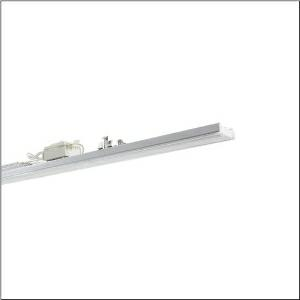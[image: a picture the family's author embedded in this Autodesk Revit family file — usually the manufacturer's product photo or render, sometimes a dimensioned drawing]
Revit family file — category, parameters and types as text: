
# Revit family: licross_r__11_recessed_ho_51te18cn4c5m_9f39
name_source: partatom
category: Lighting Fixtures
units: mm (PartAtom-declared; Revit-internal decimal feet)

## family parameters
Cut with Voids When Loaded = No
Host = Face
Light Source = No
Part Type = Normal
Room Calculation Point = No
Round Connector Dimension = Use Diameter
Shared = No

## types (1)
- --- (1 x LED, 12610 lm, 66.5 W, 4000K)
    Apparent Load = 67 VA
    CIE Flux Codes = 78 94 99 100 100
    Color Rendering = 80
    Color Temperature = 4000K
    Default Elevation = 1800 mm
    Description = Licross® 11 Recessed HO, luminaire insert, of sheet steel, galvanised, coil coated, white, length: 1.500mm, width: 66mm, height: 67mm, LED rated luminous flux: 12.610lm, light colour: 840, control gear: ON/OFF Multilumen, CLOi, with plug, 3-pole, with phase selection, mains connection: 220..240V, AC, 50/60Hz, start of lifetime: 67W, end of service life: 75W, halogen-free wiring, primary light control with lens, of plastic, primary optical cover: cover, of PMMA, light emission: direct distribution, primary light characteristic: symmetric, protection rating (complete): IP54, insulation class (complete): insulation class I (protective earthing), certification: CE, ENEC, VDE, UKCA, protection symbol: D if used in an environment with non-conductive dust loads with corresponding accessories, impact resistance: IK06, permissible ambient temperature for indoor applications: -35..+35°C, corresponds to IFS (International Featured Standards) requirements for safety and quality in the food industry, reducing of maximum allowable ambient temperature of 5°C with ceiling mounting, LABS conformity tested according to VDMA 24364:2018-05, packaging unit: 1 piece
    Height = 58 mm
    Lamp = 1 x LED
    Lamp Light Flux = 12610 lm
    Lamp Power = 66.5 W
    Lamp count = 1
    Length = 1500 mm
    Luminous efficacy = 190 lm/W
    Manufacturer = Siteco
    ModVariant = No
    Model = 51TE18CN4C5M
    Mounting Place = Ceiling
    Mounting Type = Pendant
    Number of Poles = 1
    OnlyDefault = Yes
    Power Factor = 1
    Product Name = Licross® 11 Recessed HO
    Product group = luminaire insert
    ProductGroupID = 902
    Protection Class = Protection class I
    Protection Degree = IP 54
    RLX_Detail_Level = 1
    RLX_Emergency_Light_Flux = 0 lm
    RLX_Emergency_Type = 0
    RLX_Emergency_Type_DB = No
    RlxData = <blob elided: 22309 chars, md5=1e41ee86>
    Socket = socket
    Standby Power = 0 W
    System Light Flux = 12610 lm
    System Power = 67 W
    Type Comments = factory setting: luminous flux: 100 % | (A | C | E) | 156 mA
    Type Image = l_1296930.jpg
    URL = http://relux.com
    VarID = @adj_084666
    Voltage = 0 V
    Weight = 0.00 kg
    Width = 66 mm

## geometry (parser evidence)
native form markers: Blend x4, Sweep x12
no freeform markers — native parametric forms only
